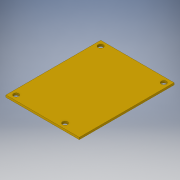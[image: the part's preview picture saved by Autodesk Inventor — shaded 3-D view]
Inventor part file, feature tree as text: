
AUTODESK INVENTOR PART (.ipt)
format: ipt  version: 2017 (Build 210142000, 142)  size: 112,640 bytes
history: native  units: in
note: dims shown in document units (in); Inventor stores cm internally (conversion verified against a paired STEP export)
features: extrude x2, sketch x2, projected_geometry x1
ambient origin geometry x8: Origin, YZ Plane, XZ Plane, XY Plane, X Axis, Y Axis, Z Axis, Center Point
bodies: Solid1 (feature_tree)
feature tree (5):
  extrude  "Extrusion1"  Depth=2.325in
  extrude  "Extrusion2"  Depth=0.05in
  sketch  "Sketch1"  dims[d0=1.8in d1=2.325in]
  sketch  "Sketch2"  dims[d2=0.05in d3=0.0in d4=0.125in d5=0.125in d6=0.125in d7=0.125in d8=0.125in d9=0.125in d10=0.475in d11=0.125in d12=0.125in d13=0.125in d14=0.125in d15=0.125in d16=0.06in d17=0.0in]
  projected_geometry  "Projected Loop1"
